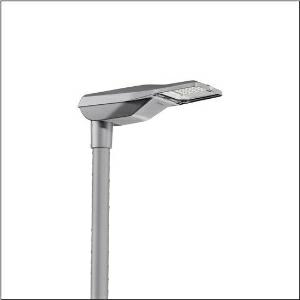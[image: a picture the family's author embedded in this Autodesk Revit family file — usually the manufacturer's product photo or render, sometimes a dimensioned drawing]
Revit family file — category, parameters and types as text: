
# Revit family: streetlight_sl_21_iq_micro___st0_8a_5xe1c31d08cb_88cc
name_source: partatom
category: Lighting Fixtures
units: mm (PartAtom-declared; Revit-internal decimal feet)

## family parameters
Cut with Voids When Loaded = No
Host = Face
Light Source = No
Part Type = Normal
Room Calculation Point = No
Round Connector Dimension = Use Diameter
Shared = No

## types (1)
- --- (1 x LED, 2870 lm, 19.4 W, 3000K)
    Apparent Load = 19 VA
    CIE Flux Codes = 38 75 97 100 100
    Color Rendering = 70
    Color Temperature = 3000K
    Default Elevation = 1800 mm
    Description = Streetlight SL 21 iQ micro, mast luminaire, primary light control with lens, of PMMA, primary optical cover: cover, of toughened safety glass, transparent, light distribution: ST0.8a, light emission: direct distribution, primary light characteristic: asymmetric, installation type: post-top, side-entry, LED, High Power LED, rated luminous flux: 2.870lm, luminous efficacy: 148lm/W, light colour: 730, colour temperature: 3000K, control gear: iQ-Comfort, control: Auto-Match, Temp-Guard, Lumen-Switch, Night-Set, Smart-Wire, Light-Fading, Desk-Remote (wireless, voltage-free reading and setting of iQ features in the workshop via application-optimized NFC function/RFID function), optimised constant luminous flux control (CLO 2.0), pre-setting: linear dimming characteristic, mains connection: 220..240V, AC, 50/60Hz, start of lifetime: 19W, end of service life: 20W, reduction: 10W, luminaire housing, of diecast aluminium, powder-coated, SITECO metallic grey (DB 702S), corrosivity category C5 high according to DIN EN ISO 12944, please order mast flange separately, inclination adjustable: 0°, 5°, 10°, 15°, sealing non-destructively replaceable, multi-level sealing system, length: 528mm, width: 235mm, height: 110mm, mast flange for spigot size: 42mm (side-entry): 5XC10008XM4, 60/48mm (side-entry/post-top): 5XC10108XM2, 76/60mm (side-entry/post-top): 5XC10108XM1, protection rating (complete): IP66, insulation class (complete): insulation class II (safety insulation), certification: CE, ENEC, ENEC+, VDE, impact resistance: IK10, permissible operating ambient temperature for outdoor applications: -40..+50°C, standard-compliant lighting for roads and squares, packaging unit: 1 piece

Light Distribution: ST0.8a
    Height = 110 mm
    Lamp = 1 x LED
    Lamp Light Flux = 2870 lm
    Lamp Power = 19.4 W
    Lamp count = 1
    Length = 528 mm
    Luminous efficacy = 148 lm/W
    Manufacturer = Siteco
    ModVariant = No
    Model = 5XE1C31D08CB
    Number of Poles = 1
    OnlyDefault = Yes
    Power Factor = 1
    Product Name = Streetlight SL 21 iQ micro | ST0.8a
    Product group = mast luminaire | pylon top
    ProductGroupID = 6100
    Protection Class = Protection class II
    Protection Degree = IP 66
    RLX_Detail_Level = 1
    RLX_Emergency_Light_Flux = 0 lm
    RLX_Emergency_Type = 0
    RLX_Emergency_Type_DB = No
    RlxData = <blob elided: 99249 chars, md5=63ed3eb6>
    Socket = socket
    Standby Power = 0 W
    System Light Flux = 2870 lm
    System Power = 19 W
    Type Comments = factory setting: luminous flux: 100 % | dim-lin: 254 | 387 mA
    Type Image = l_1006881.jpg
    URL = http://relux.com
    VarID = @adj_137959
    Voltage = 0 V
    Weight = 0.00 kg
    Width = 235 mm

## geometry (parser evidence)
native form markers: Blend x4, Sweep x11
no freeform markers — native parametric forms only
